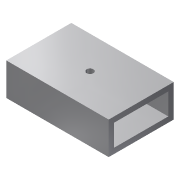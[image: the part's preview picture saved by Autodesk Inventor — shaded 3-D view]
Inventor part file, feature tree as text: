
AUTODESK INVENTOR PART (.ipt)
format: ipt  version: 2014 (Build 180170000, 170)  size: 88,064 bytes
history: native  units: mm
features: extrude x2, sketch x2
ambient origin geometry x8: Origin, YZ Plane, XZ Plane, XY Plane, X Axis, Y Axis, Z Axis, Center Point
bodies: Solid1 (feature_tree)
feature tree (4):
  extrude  "Extrusion1"  Depth=19.05mm
  extrude  "Extrusion2"  Depth=3.175mm
  sketch  "Sketch1"  dims[d0=38.1mm d1=19.05mm]
  sketch  "Sketch2"  dims[d2=3.175mm d3=3.175mm d4=60.0mm d5=0.0mm d6=4.0mm d7=10.0mm d8=0.0mm]
